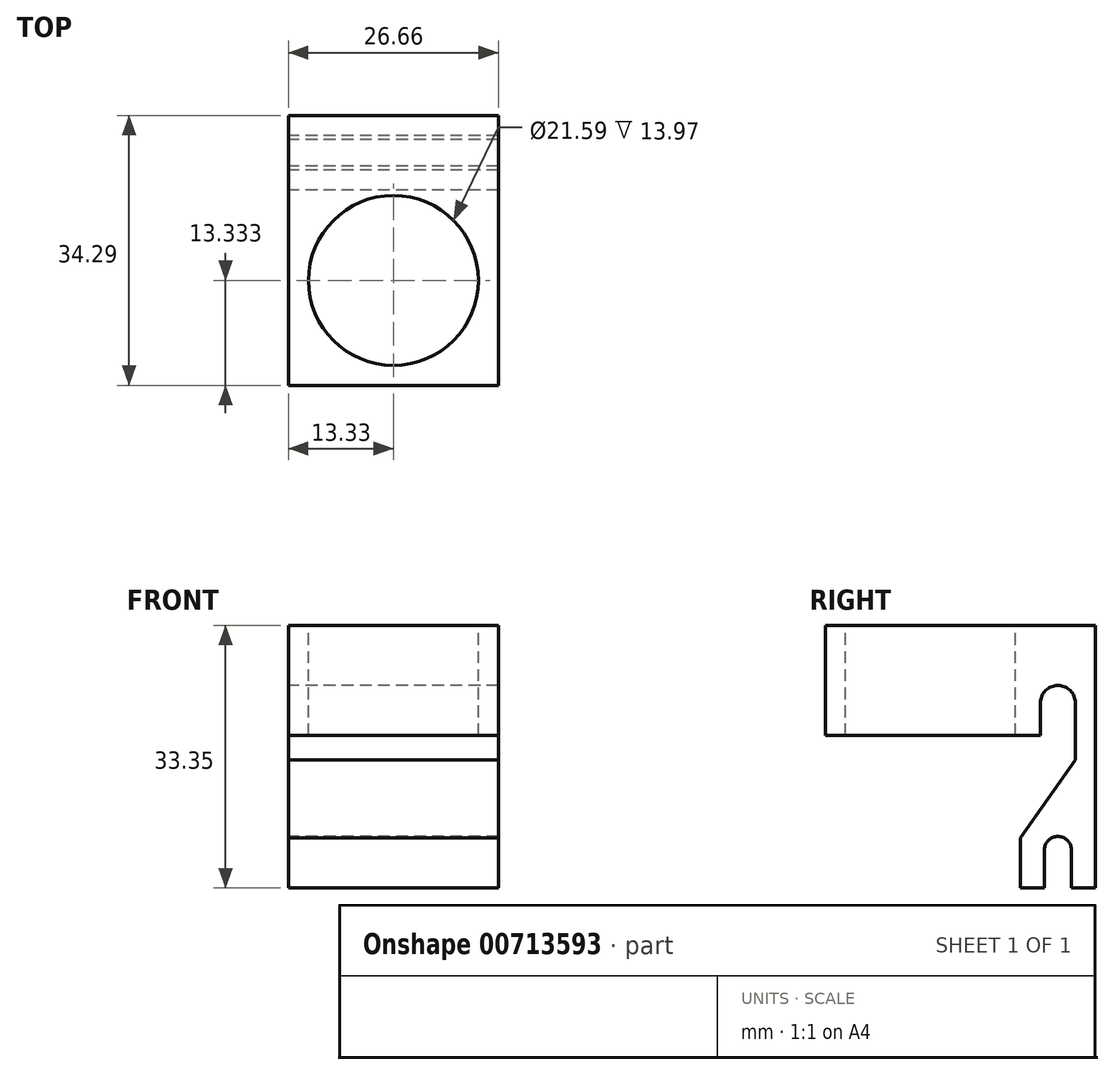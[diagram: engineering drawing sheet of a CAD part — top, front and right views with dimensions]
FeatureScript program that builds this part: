
annotation { "Feature Type Name" : "Feature", "Feature Type Description" : "" }
export const myFeature = defineFeature(function(context is Context, id is Id, definition is map)
    precondition{}
    {
        {
            var Q0;
            Q0=qCreatedBy(makeId("Right.planeOp"),FACE);
            var sketch = newSketch(context, id + "F0", { "sketchPlane" : qUnion([Q0])});
            skLineSegment(sketch, "E0", {"start": v(-31.24, 0) * mm, "end": v(3.05, 0) * mm});
            skLineSegment(sketch, "E1", {"start": v(3.05, 0) * mm, "end": v(3.05, -33.35) * mm});
            skLineSegment(sketch, "E2", {"start": v(3.05, -33.35) * mm, "end": v(0, -33.35) * mm});
            skLineSegment(sketch, "E3", {"start": v(0, -33.35) * mm, "end": v(0, -28.5) * mm});
            skLineSegment(sketch, "E4", {"start": v(-3.4, -28.5) * mm, "end": v(-3.4, -33.35) * mm});
            skLineSegment(sketch, "E5", {"start": v(-3.4, -33.35) * mm, "end": v(-6.45, -33.35) * mm});
            skLineSegment(sketch, "E6", {"start": v(-6.45, -33.35) * mm, "end": v(-6.45, -27) * mm});
            skLineSegment(sketch, "E7", {"start": v(-6.45, -27) * mm, "end": v(0.5, -17.06) * mm});
            skLineSegment(sketch, "E8", {"start": v(-3.91, -9.83) * mm, "end": v(-3.91, -13.97) * mm});
            skLineSegment(sketch, "E9", {"start": v(-3.91, -13.97) * mm, "end": v(-31.24, -13.97) * mm});
            skLineSegment(sketch, "E10", {"start": v(-31.24, -13.97) * mm, "end": v(-31.24, 0) * mm});
            skArc(sketch, "E11", {"start": v(0.5, -9.83) * mm, "mid": v(-1.7, -7.62) * mm, "end": v(-3.91, -9.83) * mm});
            skArc(sketch, "E12", {"start": v(0, -28.5) * mm, "mid": v(-1.7, -26.8) * mm, "end": v(-3.4, -28.5) * mm});
            skLineSegment(sketch, "E13", {"start": v(0.5, -9.83) * mm, "end": v(0.5, -17.06) * mm});
            skLineSegment(sketch, "E14", {"start": v(-1.7, -9.83) * mm, "end": v(-1.7, -28.5) * mm, "construction": true});
            skSolve(sketch);
        }
        {
            var Q0;
            Q0=makeQuery(id+"F0.imprint","IMPRINT",FACE,{"disambiguationData":[TD([[makeQuery(id+"F0.imprint","IMPRINT",EDGE,{"derivedFrom":sQuery(id+"F0.wireOp",EDGE,"E0")}),-1.0]])]});
            extrude(context, id + "F1", {"entities" : qUnion([Q0]), "endBound" : BoundingType.SYMMETRIC, "depth" : 26.67 * mm, "offsetDistance" : 25.4 * mm});
        }
        {
            var Q0;
            Q0=qCreatedBy(makeId("Top.planeOp"),FACE);
            var sketch = newSketch(context, id + "F2", { "sketchPlane" : qUnion([Q0])});
            skCircle(sketch, "E15", {"center": v(0, -17.9) * mm, "radius": 10.8 * mm});
            skSolve(sketch);
        }
        {
            var Q0;
            Q0=makeQuery(id+"F2.imprint","IMPRINT",FACE,{"disambiguationData":[TD([[makeQuery(id+"F2.imprint","IMPRINT",EDGE,{"derivedFrom":sQuery(id+"F2.wireOp",EDGE,"E15")}),1.0]])]});
            extrude(context, id + "F3", {"entities" : qUnion([Q0]), "operationType" : NewBodyOperationType.REMOVE, "endBound" : BoundingType.THROUGH_ALL, "oppositeDirection" : true, "depth" : 25.4 * mm, "offsetDistance" : 25.4 * mm});
        }
    });
